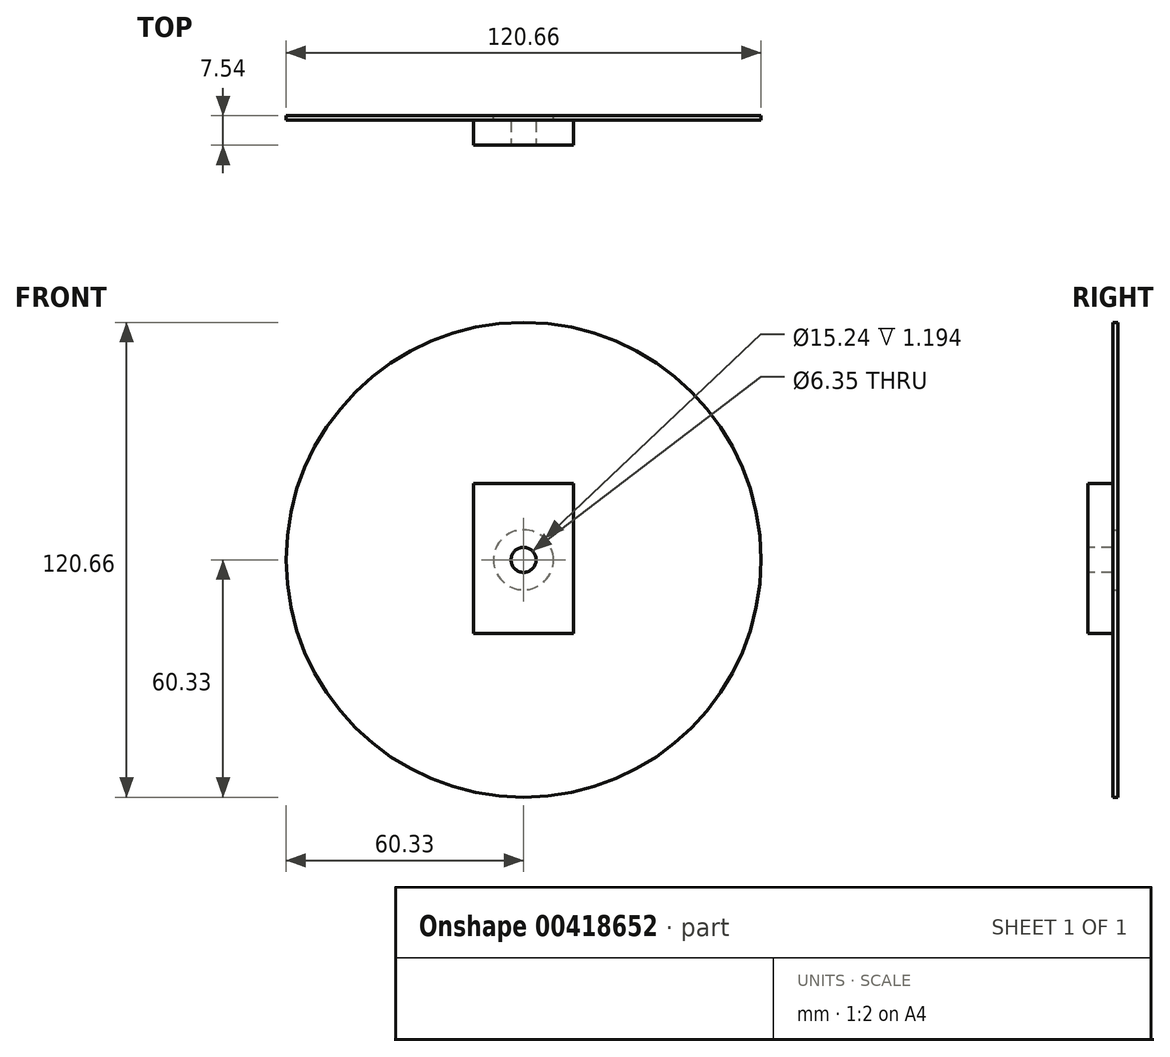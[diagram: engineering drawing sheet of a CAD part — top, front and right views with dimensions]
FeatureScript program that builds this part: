
annotation { "Feature Type Name" : "Feature", "Feature Type Description" : "" }
export const myFeature = defineFeature(function(context is Context, id is Id, definition is map)
    precondition{}
    {
        {
            var Q0;
            Q0=qCreatedBy(makeId("Front.planeOp"),FACE);
            var sketch = newSketch(context, id + "F0", { "sketchPlane" : qUnion([Q0])});
            skCircle(sketch, "E0", {"center": v(0, 0) * mm, "radius": 60.33 * mm});
            skCircle(sketch, "E1", {"center": v(0, 0) * mm, "radius": 7.62 * mm});
            skSolve(sketch);
        }
        {
            var Q0;
            Q0 = qSketchRegion(id + "F0", true);
            var Q1;
            Q1=makeQuery(id+"F0.imprint","IMPRINT",FACE,{"disambiguationData":[TD([[makeQuery(id+"F0.imprint","IMPRINT",EDGE,{"derivedFrom":sQuery(id+"F0.wireOp",EDGE,"E0")}),1.0]])]});
            extrude(context, id + "F1", {"entities" : qUnion([Q0, Q1]), "depth" : 1.2 * mm});
        }
        {
            var Q0;
            Q0=makeQuery(id+"F1.opExtrude","CAP_FACE",FACE,{"disambiguationData":[OSD([sQuery(id+"F0.wireOp",EDGE,"E0"),sQuery(id+"F0.wireOp",EDGE,"E1")])],"isStart":false});
            var sketch = newSketch(context, id + "F2", { "sketchPlane" : qUnion([Q0])});
            skLineSegment(sketch, "E2.bottom", {"start": v(0, 19.4) * mm, "end": v(12.7, 19.4) * mm});
            skLineSegment(sketch, "E3", {"start": v(0, 19.4) * mm, "end": v(-12.7, 19.4) * mm});
            skLineSegment(sketch, "E4", {"start": v(-12.7, 19.4) * mm, "end": v(-12.7, -18.7) * mm});
            skLineSegment(sketch, "E5", {"start": v(-12.7, -18.7) * mm, "end": v(12.7, -18.7) * mm});
            skLineSegment(sketch, "E6", {"start": v(12.7, 19.4) * mm, "end": v(12.7, -18.7) * mm});
            skSolve(sketch);
        }
        {
            var Q0;
            Q0=makeQuery(id+"F2.imprint","IMPRINT",FACE,{"disambiguationData":[TD([[makeQuery(id+"F2.imprint","IMPRINT",EDGE,{"derivedFrom":sQuery(id+"F2.wireOp",EDGE,"E2.bottom")}),-1.0]])]});
            var Q1;
            Q1=makeQuery(id+"F2.imprint","IMPRINT",FACE,{"disambiguationData":[TD([[makeQuery(id+"F2.imprint","IMPRINT",EDGE,{"derivedFrom":makeQuery(id+"F1.opExtrude","CAP_EDGE",EDGE,{"disambiguationData":[OSD([sQuery(id+"F0.wireOp",EDGE,"E1")])],"isStart":false})}),1.0]])]});
            extrude(context, id + "F3", {"entities" : qUnion([Q0, Q1]), "operationType" : NewBodyOperationType.ADD, "depth" : 6.35 * mm, "offsetDistance" : 25.4 * mm});
        }
        {
            var Q0;
            Q0=makeQuery(id+"F3.opExtrude","CAP_FACE",FACE,{"disambiguationData":[OSD([sQuery(id+"F2.wireOp",EDGE,"E2.bottom"),sQuery(id+"F2.wireOp",EDGE,"E3"),sQuery(id+"F2.wireOp",EDGE,"E4"),sQuery(id+"F2.wireOp",EDGE,"E5"),sQuery(id+"F2.wireOp",EDGE,"E6")])],"isStart":false});
            var sketch = newSketch(context, id + "F4", { "sketchPlane" : qUnion([Q0])});
            skCircle(sketch, "E7", {"center": v(0, 0) * mm, "radius": 3.18 * mm});
            skSolve(sketch);
        }
        {
            var Q0;
            Q0=makeQuery(id+"F4.imprint","IMPRINT",FACE,{"disambiguationData":[TD([[makeQuery(id+"F4.imprint","IMPRINT",EDGE,{"derivedFrom":sQuery(id+"F4.wireOp",EDGE,"E7")}),1.0]])]});
            extrude(context, id + "F5", {"entities" : qUnion([Q0]), "operationType" : NewBodyOperationType.REMOVE, "oppositeDirection" : true, "depth" : 25.4 * mm, "offsetDistance" : 25.4 * mm});
        }
    });
